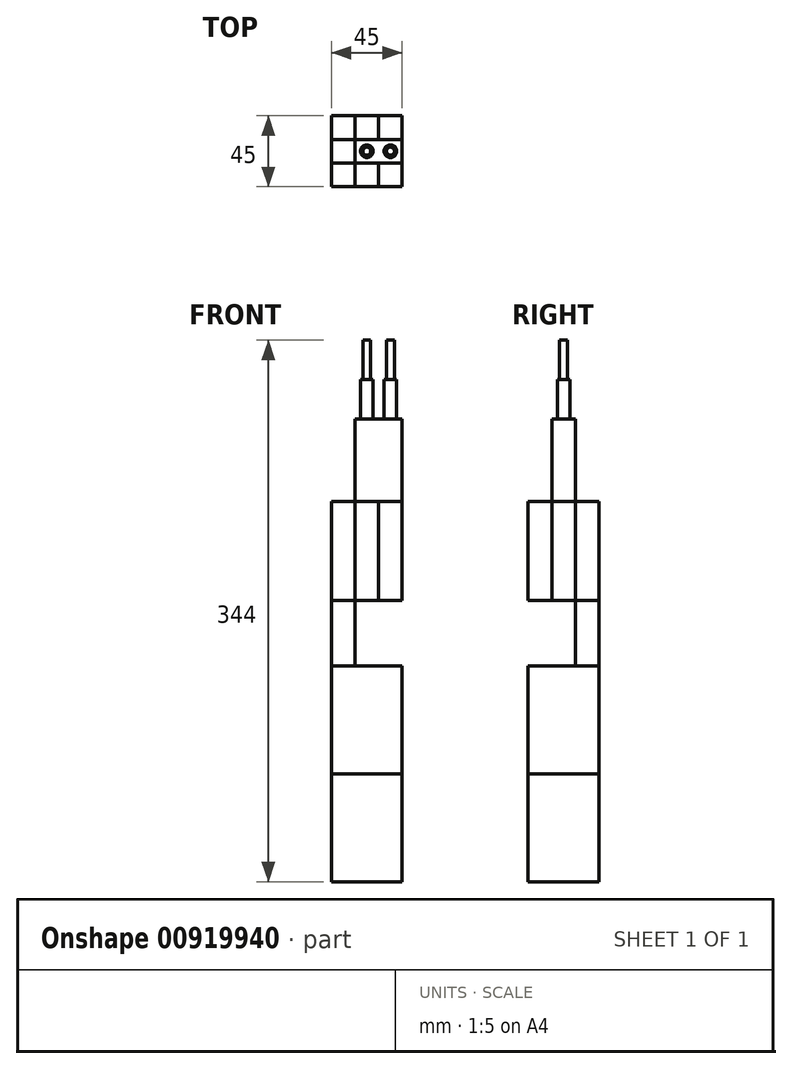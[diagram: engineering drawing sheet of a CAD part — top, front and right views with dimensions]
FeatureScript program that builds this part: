
annotation { "Feature Type Name" : "Feature", "Feature Type Description" : "" }
export const myFeature = defineFeature(function(context is Context, id is Id, definition is map)
    precondition{}
    {
        {
            var Q0;
            Q0=qCreatedBy(makeId("Top.planeOp"),FACE);
            var sketch = newSketch(context, id + "F0", { "sketchPlane" : qUnion([Q0])});
            skLineSegment(sketch, "E0.bottom", {"start": v(0, 0) * mm, "end": v(45, 0) * mm});
            skLineSegment(sketch, "E0.top", {"start": v(0, -45) * mm, "end": v(45, -45) * mm});
            skLineSegment(sketch, "E0.left", {"start": v(0, 0) * mm, "end": v(0, -45) * mm});
            skLineSegment(sketch, "E0.right", {"start": v(45, 0) * mm, "end": v(45, -45) * mm});
            skSolve(sketch);
        }
        {
            var Q0;
            Q0=makeQuery(id+"F0.imprint","IMPRINT",FACE,{"disambiguationData":[TD([[makeQuery(id+"F0.imprint","IMPRINT",EDGE,{"derivedFrom":sQuery(id+"F0.wireOp",EDGE,"E0.bottom")}),-1.0]])]});
            extrude(context, id + "F1", {"entities" : qUnion([Q0]), "depth" : 68.5 * mm, "offsetDistance" : 25 * mm});
        }
        {
            var Q0;
            Q0=makeQuery(id+"F1.opExtrude","CAP_FACE",FACE,{"disambiguationData":[OSD([sQuery(id+"F0.wireOp",EDGE,"E0.bottom"),sQuery(id+"F0.wireOp",EDGE,"E0.top"),sQuery(id+"F0.wireOp",EDGE,"E0.left"),sQuery(id+"F0.wireOp",EDGE,"E0.right")])],"isStart":false});
            extrude(context, id + "F2", {"entities" : qUnion([Q0]), "depth" : 68.5 * mm, "offsetDistance" : 25 * mm});
        }
        {
            var Q0;
            Q0=makeQuery(id+"F2.opExtrude","CAP_FACE",FACE,{"disambiguationData":[OSD([sQuery(id+"F0.wireOp",EDGE,"E0.bottom"),sQuery(id+"F0.wireOp",EDGE,"E0.top"),sQuery(id+"F0.wireOp",EDGE,"E0.left"),sQuery(id+"F0.wireOp",EDGE,"E0.right")])],"isStart":false});
            var sketch = newSketch(context, id + "F3", { "sketchPlane" : qUnion([Q0])});
            skLineSegment(sketch, "E1.bottom", {"start": v(0, 0) * mm, "end": v(45, 0) * mm});
            skLineSegment(sketch, "E1.top", {"start": v(0, -45) * mm, "end": v(45, -45) * mm});
            skLineSegment(sketch, "E1.left", {"start": v(0, 0) * mm, "end": v(0, -45) * mm});
            skLineSegment(sketch, "E1.right", {"start": v(45, 0) * mm, "end": v(45, -45) * mm});
            skLineSegment(sketch, "E2.bottom", {"start": v(45, -45) * mm, "end": v(30, -45) * mm});
            skLineSegment(sketch, "E2.top", {"start": v(45, -30) * mm, "end": v(30, -30) * mm});
            skLineSegment(sketch, "E2.left", {"start": v(45, -45) * mm, "end": v(45, -30) * mm});
            skLineSegment(sketch, "E2.right", {"start": v(30, -45) * mm, "end": v(30, -30) * mm});
            skLineSegment(sketch, "E3.bottom", {"start": v(0, 0) * mm, "end": v(15, 0) * mm});
            skLineSegment(sketch, "E3.top", {"start": v(0, -15) * mm, "end": v(15, -15) * mm});
            skLineSegment(sketch, "E3.left", {"start": v(0, 0) * mm, "end": v(0, -15) * mm});
            skLineSegment(sketch, "E3.right", {"start": v(15, 0) * mm, "end": v(15, -15) * mm});
            skSolve(sketch);
        }
        {
            var Q0;
            Q0=makeQuery(id+"F3.imprint","IMPRINT",FACE,{"disambiguationData":[TD([[makeQuery(id+"F3.imprint","IMPRINT",EDGE,{"derivedFrom":sQuery(id+"F3.wireOp",EDGE,"E1.bottom")}),-1.0]])]});
            extrude(context, id + "F4", {"entities" : qUnion([Q0]), "depth" : 41.5 * mm, "offsetDistance" : 25 * mm});
        }
        {
            var Q0;
            Q0=makeQuery(id+"F4.opExtrude","CAP_FACE",FACE,{"disambiguationData":[OSD([sQuery(id+"F3.wireOp",EDGE,"E1.bottom"),sQuery(id+"F3.wireOp",EDGE,"E1.top"),sQuery(id+"F3.wireOp",EDGE,"E1.left"),sQuery(id+"F3.wireOp",EDGE,"E1.right"),sQuery(id+"F3.wireOp",EDGE,"E2.top"),sQuery(id+"F3.wireOp",EDGE,"E2.right"),sQuery(id+"F3.wireOp",EDGE,"E3.top"),sQuery(id+"F3.wireOp",EDGE,"E3.right")])],"isStart":false});
            var sketch = newSketch(context, id + "F5", { "sketchPlane" : qUnion([Q0])});
            skLineSegment(sketch, "E4.bottom", {"start": v(0, -15) * mm, "end": v(45, -15) * mm});
            skLineSegment(sketch, "E4.top", {"start": v(0, -30) * mm, "end": v(45, -30) * mm});
            skLineSegment(sketch, "E4.left", {"start": v(0, -15) * mm, "end": v(0, -30) * mm});
            skLineSegment(sketch, "E4.right", {"start": v(45, -15) * mm, "end": v(45, -30) * mm});
            skLineSegment(sketch, "E5.bottom", {"start": v(15, 0) * mm, "end": v(30, 0) * mm});
            skLineSegment(sketch, "E5.top", {"start": v(15, -45) * mm, "end": v(30, -45) * mm});
            skLineSegment(sketch, "E5.left", {"start": v(15, 0) * mm, "end": v(15, -45) * mm});
            skLineSegment(sketch, "E5.right", {"start": v(30, 0) * mm, "end": v(30, -45) * mm});
            skSolve(sketch);
        }
        {
            var Q0;
            {var subQ5=sQuery(id+"F5.wireOp",EDGE,"E5.bottom");Q0=makeQuery(id+"F5.imprint","IMPRINT",FACE,{"disambiguationData":[TD([[makeQuery(id+"F5.imprint","IMPRINT",EDGE,{"derivedFrom":subQ5}),-1.0]])]});}
            var Q1;
            {var subQ0=sQuery(id+"F5.wireOp",EDGE,"E5.left");var subQ1=sQuery(id+"F5.wireOp",EDGE,"E4.bottom");var subQ2=makeQuery(id+"F5.imprint","INTERSECT",VERTEX,{"derivedFrom":[subQ1,subQ0]});Q1=makeQuery(id+"F5.imprint","IMPRINT",FACE,{"disambiguationData":[TD([[makeQuery(id+"F5.imprint","IMPRINT",EDGE,{"disambiguationData":[TD([[subQ2,-1.0]])],"derivedFrom":subQ1}),-1.0]])]});}
            var Q2;
            {var subQ0=sQuery(id+"F5.wireOp",EDGE,"E4.left");Q2=makeQuery(id+"F5.imprint","IMPRINT",FACE,{"disambiguationData":[TD([[makeQuery(id+"F5.imprint","IMPRINT",EDGE,{"derivedFrom":subQ0}),1.0]])]});}
            var Q3;
            {var subQ5=sQuery(id+"F5.wireOp",EDGE,"E5.top");Q3=makeQuery(id+"F5.imprint","IMPRINT",FACE,{"disambiguationData":[TD([[makeQuery(id+"F5.imprint","IMPRINT",EDGE,{"derivedFrom":subQ5}),1.0]])]});}
            var Q4;
            {var subQ0=sQuery(id+"F5.wireOp",EDGE,"E4.right");Q4=makeQuery(id+"F5.imprint","IMPRINT",FACE,{"disambiguationData":[TD([[makeQuery(id+"F5.imprint","IMPRINT",EDGE,{"derivedFrom":subQ0}),-1.0]])]});}
            extrude(context, id + "F6", {"entities" : qUnion([Q0, Q1, Q2, Q3, Q4]), "depth" : 63 * mm, "offsetDistance" : 25 * mm});
        }
        {
            var Q0;
            Q0=makeQuery(id+"F6.opExtrude","CAP_FACE",FACE,{"disambiguationData":[OSD([sQuery(id+"F5.wireOp",EDGE,"E4.bottom"),sQuery(id+"F5.wireOp",EDGE,"E4.top"),sQuery(id+"F5.wireOp",EDGE,"E4.left"),sQuery(id+"F5.wireOp",EDGE,"E4.right"),sQuery(id+"F5.wireOp",EDGE,"E5.bottom"),sQuery(id+"F5.wireOp",EDGE,"E5.top"),sQuery(id+"F5.wireOp",EDGE,"E5.left"),sQuery(id+"F5.wireOp",EDGE,"E5.right")])],"isStart":false});
            var sketch = newSketch(context, id + "F7", { "sketchPlane" : qUnion([Q0])});
            skLineSegment(sketch, "E6.bottom", {"start": v(45, -15) * mm, "end": v(15, -15) * mm});
            skLineSegment(sketch, "E6.top", {"start": v(45, -30) * mm, "end": v(15, -30) * mm});
            skLineSegment(sketch, "E6.left", {"start": v(45, -15) * mm, "end": v(45, -30) * mm});
            skLineSegment(sketch, "E6.right", {"start": v(15, -15) * mm, "end": v(15, -30) * mm});
            skSolve(sketch);
        }
        {
            var Q0;
            {var subQ9=sQuery(id+"F7.wireOp",EDGE,"E6.left");Q0=makeQuery(id+"F7.imprint","IMPRINT",FACE,{"disambiguationData":[TD([[makeQuery(id+"F7.imprint","IMPRINT",EDGE,{"derivedFrom":subQ9}),-1.0]])]});}
            extrude(context, id + "F8", {"entities" : qUnion([Q0]), "depth" : 52.5 * mm, "offsetDistance" : 25 * mm});
        }
        {
            var Q0;
            Q0=makeQuery(id+"F8.opExtrude","CAP_FACE",FACE,{"disambiguationData":[OSD([sQuery(id+"F7.wireOp",EDGE,"E6.bottom"),sQuery(id+"F7.wireOp",EDGE,"E6.top"),sQuery(id+"F7.wireOp",EDGE,"E6.left"),sQuery(id+"F7.wireOp",EDGE,"E6.right")])],"isStart":false});
            var sketch = newSketch(context, id + "F9", { "sketchPlane" : qUnion([Q0])});
            skLineSegment(sketch, "E7.0.0", {"start": v(30, -15) * mm, "end": v(30, 0) * mm});
            skLineSegment(sketch, "E7.0.1", {"start": v(30, 0) * mm, "end": v(15, 0) * mm});
            skLineSegment(sketch, "E7.0.2", {"start": v(15, 0) * mm, "end": v(15, -15) * mm});
            skLineSegment(sketch, "E7.0.3", {"start": v(15, -15) * mm, "end": v(0, -15) * mm});
            skLineSegment(sketch, "E7.0.4", {"start": v(0, -15) * mm, "end": v(0, -30) * mm});
            skLineSegment(sketch, "E7.0.5", {"start": v(0, -30) * mm, "end": v(15, -30) * mm});
            skLineSegment(sketch, "E7.0.6", {"start": v(15, -30) * mm, "end": v(15, -45) * mm});
            skLineSegment(sketch, "E7.0.7", {"start": v(15, -45) * mm, "end": v(30, -45) * mm});
            skLineSegment(sketch, "E7.0.8", {"start": v(30, -45) * mm, "end": v(30, -30) * mm});
            skLineSegment(sketch, "E7.0.9", {"start": v(30, -30) * mm, "end": v(45, -30) * mm});
            skLineSegment(sketch, "E7.0.10", {"start": v(45, -30) * mm, "end": v(45, -15) * mm});
            skLineSegment(sketch, "E7.0.11", {"start": v(45, -15) * mm, "end": v(30, -15) * mm});
            skCircle(sketch, "E8", {"center": v(22.5, -22.5) * mm, "radius": 4 * mm});
            skPoint(sketch, "E8.centerSnap0", {"position": v(15, -22.5) * mm});
            skPoint(sketch, "E8.centerSnap1", {"position": v(22.5, 0) * mm});
            skCircle(sketch, "E9", {"center": v(37.5, -22.5) * mm, "radius": 4 * mm});
            skPoint(sketch, "E9.centerSnap0", {"position": v(37.5, -15) * mm});
            skSolve(sketch);
        }
        {
            var Q0;
            Q0=makeQuery(id+"F9.imprint","IMPRINT",FACE,{"disambiguationData":[TD([[makeQuery(id+"F9.imprint","IMPRINT",EDGE,{"derivedFrom":sQuery(id+"F9.wireOp",EDGE,"E8")}),1.0]])]});
            var Q1;
            Q1=makeQuery(id+"F9.imprint","IMPRINT",FACE,{"disambiguationData":[TD([[makeQuery(id+"F9.imprint","IMPRINT",EDGE,{"derivedFrom":sQuery(id+"F9.wireOp",EDGE,"E9")}),1.0]])]});
            extrude(context, id + "F10", {"entities" : qUnion([Q0, Q1]), "depth" : 25 * mm, "offsetDistance" : 25 * mm});
        }
        {
            var Q0;
            Q0=makeQuery(id+"F10.opExtrude","CAP_FACE",FACE,{"disambiguationData":[OSD([sQuery(id+"F9.wireOp",EDGE,"E8")])],"isStart":false});
            var sketch = newSketch(context, id + "F11", { "sketchPlane" : qUnion([Q0])});
            skCircle(sketch, "E10", {"center": v(22.5, -22.5) * mm, "radius": 2.5 * mm});
            skCircle(sketch, "E11.0.0", {"center": v(37.5, -22.5) * mm, "radius": 4 * mm});
            skCircle(sketch, "E12", {"center": v(37.5, -22.5) * mm, "radius": 2.5 * mm});
            skSolve(sketch);
        }
        {
            var Q0;
            Q0=makeQuery(id+"F11.imprint","IMPRINT",FACE,{"disambiguationData":[TD([[makeQuery(id+"F11.imprint","IMPRINT",EDGE,{"derivedFrom":sQuery(id+"F11.wireOp",EDGE,"E10")}),1.0]])]});
            var Q1;
            Q1=makeQuery(id+"F11.imprint","IMPRINT",FACE,{"disambiguationData":[TD([[makeQuery(id+"F11.imprint","IMPRINT",EDGE,{"derivedFrom":sQuery(id+"F11.wireOp",EDGE,"E12")}),1.0]])]});
            extrude(context, id + "F12", {"entities" : qUnion([Q0, Q1]), "operationType" : NewBodyOperationType.ADD, "depth" : 25 * mm, "offsetDistance" : 25 * mm});
        }
    });
